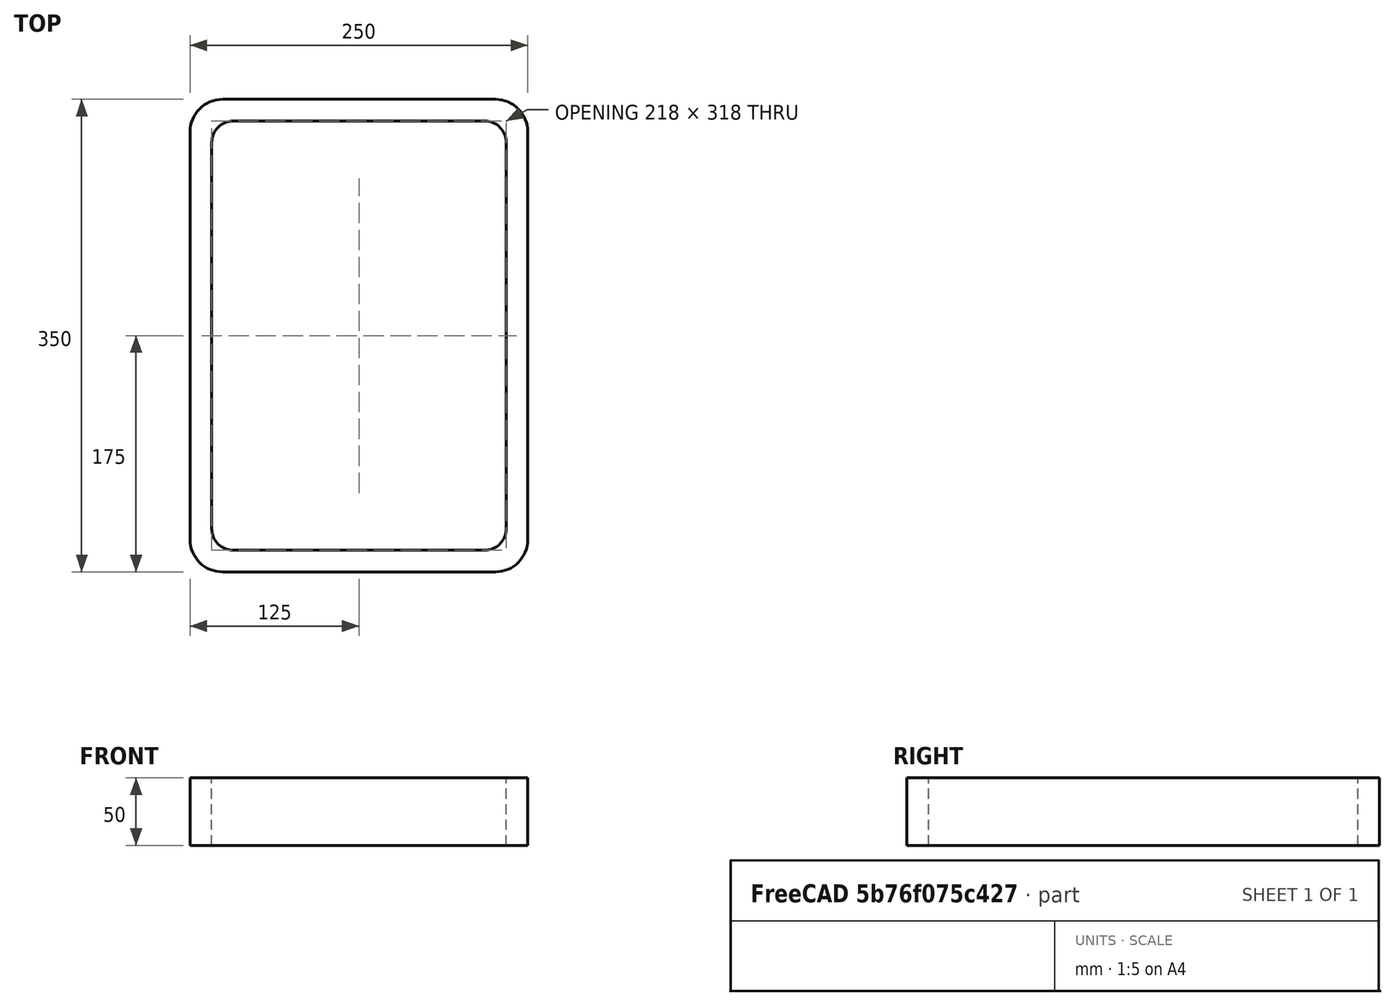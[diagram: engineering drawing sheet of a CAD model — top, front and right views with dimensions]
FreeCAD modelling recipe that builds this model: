
FCSTD DOCUMENT  (FreeCAD 0.15R4671 (Git))
Label: Rectangular hollow section 350x250x16 EN10219 S235JRH
License: All rights reserved
LicenseURL: http://en.wikipedia.org/wiki/All_rights_reserved
objects: Sketcher::SketchObject×1, Part::Extrusion×1
note: 2 computed .brp shape members not serialized (recipe doc carries the construction recipe); baked Part::Feature solids carry a one-line shape summary decoded from their .brp

FEATURE [Sketcher::SketchObject] Sketch
  sketch-geometry (16):
    g0: LineSegment StartX=-93 StartY=159 StartZ=0 EndX=93 EndY=159 EndZ=0
    g1: LineSegment StartX=109 StartY=143 StartZ=0 EndX=109 EndY=-143 EndZ=0
    g2: LineSegment StartX=93 StartY=-159 StartZ=0 EndX=-93 EndY=-159 EndZ=0
    g3: LineSegment StartX=-109 StartY=-143 StartZ=0 EndX=-109 EndY=143 EndZ=0
    g4: LineSegment StartX=-101 StartY=175 StartZ=0 EndX=101 EndY=175 EndZ=0
    g5: LineSegment StartX=125 StartY=151 StartZ=0 EndX=125 EndY=-151 EndZ=0
    g6: LineSegment StartX=101 StartY=-175 StartZ=0 EndX=-101 EndY=-175 EndZ=0
    g7: LineSegment StartX=-125 StartY=-151 StartZ=0 EndX=-125 EndY=151 EndZ=0
    g8: ArcOfCircle CenterX=-93 CenterY=143 CenterZ=0 NormalX=0 NormalY=0 NormalZ=1 Radius=16 StartAngle=1.5708 EndAngle=3.14159
    g9: ArcOfCircle CenterX=93 CenterY=143 CenterZ=0 NormalX=0 NormalY=0 NormalZ=1 Radius=16 StartAngle=0 EndAngle=1.5708
    g10: ArcOfCircle CenterX=93 CenterY=-143 CenterZ=0 NormalX=0 NormalY=0 NormalZ=1 Radius=16 StartAngle=4.71239 EndAngle=6.28319
    g11: ArcOfCircle CenterX=-93 CenterY=-143 CenterZ=0 NormalX=0 NormalY=0 NormalZ=1 Radius=16 StartAngle=3.14159 EndAngle=4.71239
    g12: ArcOfCircle CenterX=101 CenterY=151 CenterZ=0 NormalX=0 NormalY=0 NormalZ=1 Radius=24 StartAngle=0 EndAngle=1.5708
    g13: ArcOfCircle CenterX=101 CenterY=-151 CenterZ=0 NormalX=0 NormalY=0 NormalZ=1 Radius=24 StartAngle=4.71239 EndAngle=6.28319
    g14: ArcOfCircle CenterX=-101 CenterY=-151 CenterZ=0 NormalX=0 NormalY=0 NormalZ=1 Radius=24 StartAngle=3.14159 EndAngle=4.71239
    g15: ArcOfCircle CenterX=-101 CenterY=151 CenterZ=0 NormalX=0 NormalY=0 NormalZ=1 Radius=24 StartAngle=1.5708 EndAngle=3.14159
  constraints (36):
    c: Horizontal(g2)
    c: Vertical(g3)
    c: Horizontal(g6)
    c: Vertical(g7)
    c: Tangent(g3,g8) = 1.5708
    c: Tangent(g0,g8) = 1.5708
    c: Tangent(g0,g9) = 1.5708
    c: Tangent(g1,g9) = 1.5708
    c: Tangent(g1,g10) = 1.5708
    c: Tangent(g2,g10) = 1.5708
    c: Tangent(g2,g11) = 1.5708
    c: Tangent(g3,g11) = 1.5708
    c: Tangent(g4,g12) = 1.5708
    c: Tangent(g5,g12) = 1.5708
    c: Tangent(g5,g13) = 1.5708
    c: Tangent(g6,g13) = 1.5708
    c: Tangent(g6,g14) = 1.5708
    c: Tangent(g7,g14) = 1.5708
    c: Tangent(g7,g15) = 1.5708
    c: Tangent(g4,g15) = 1.5708
    c: Equal(g9,g8)
    c: Equal(g9,g11)
    c: Equal(g9,g10)
    c: Equal(g12,g15)
    c: Equal(g12,g14)
    c: Equal(g12,g13)
    c: Symmetric(g4,g6,g-1)
    c: Symmetric(g7,g5,g-2)
    c: DistanceY(g4,g6) = -350
    c: DistanceX(g7,g5) = 250
    c: Symmetric(g3,g1,g-2)
    c: Symmetric(g0,g2,g-1)
    c: DistanceY(g0,g4) = 16
    c: DistanceX(g5,g1) = -16
    c: Radius(g9) = 16
    c: Radius(g12) = 24
FEATURE [Part::Extrusion] Extrude  label="Rectangular hollow section 350x250x16 EN10219 S235JRH"
  Base = -> Sketch
  Dir = (0,0,50)
  Solid = true
